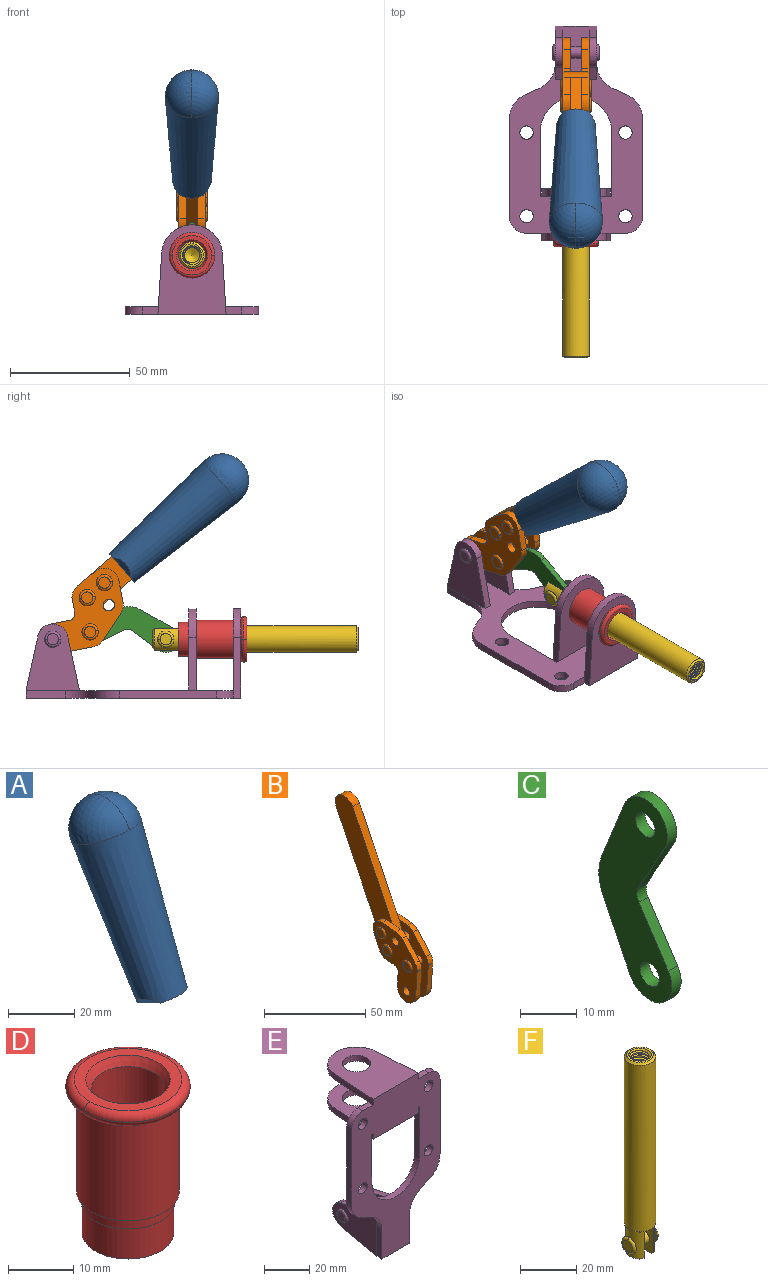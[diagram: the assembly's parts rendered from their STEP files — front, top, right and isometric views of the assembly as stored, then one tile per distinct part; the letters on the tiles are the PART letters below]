
ASSEMBLY  parts=6 mates=6
PART A: 11 faces, bbox 22.3x42.6x64.5 mm
  f0: sphere r=11.13mm, area 411.4mm2, adj f1,f8
  f1: cone r=11.11mm half-angle=3.3deg, axis (0,0.44,0.9), area 3251.8mm2, adj f0,f7,f8,f9,f10
  f2: cylinder r=6.16mm len=11.7mm, axis (1,0,0), area 89.5mm2, adj f3,f4,f5,f6
  f3: plane 60.23x36.75mm, normal (-1,0,0), area 763.6mm2, adj f2,f4,f6,f10
  f4: plane 51.37x25.05mm, normal (0,0.9,-0.44), area 264.2mm2, adj f2,f3,f5,f10
  f5: plane 60.23x36.75mm, normal (1,0,0), area 763.6mm2, adj f2,f4,f6,f10
  f6: plane 51.37x25.05mm, normal (0,-0.9,0.44), area 264.2mm2, adj f2,f3,f5,f10
  f7: plane 9.95x5.95mm, normal (0.71,-0.31,-0.64), area 25.8mm2, adj f1,f10
  f8: sphere r=11.13mm, area 411.4mm2, adj f0,f1
  f9: plane 9.95x5.95mm, normal (-0.71,-0.31,-0.64), area 25.8mm2, adj f1,f10
  f10: plane 14.27x11.38mm, normal (0,-0.44,-0.9), area 106.7mm2, adj f1,f3,f4,f5,f6,f7,f9
PART B: 59 faces, bbox 12.9x60.2x99.6 mm
  f0: torus R=2.39mm, axis (-1,0,0), area 14.9mm2, adj f20,f43,f51
  f1: torus R=2.39mm, axis (-1,0,0), area 14.9mm2, adj f19,f42,f51
  f2: torus R=2.39mm, axis (-1,0,0), area 14.9mm2, adj f18,f35,f51
  f3: torus R=2.39mm, axis (-1,0,0), area 14.9mm2, adj f14,f17,f23
  f4: torus R=2.39mm, axis (-1,0,0), area 14.9mm2, adj f13,f16,f23
  f5: torus R=2.39mm, axis (-1,0,0), area 14.9mm2, adj f12,f15,f23
  f6: cylinder r=2.39mm len=4.78mm, axis (1,0,0), area 46.5mm2, adj f48,f50,f51
  f7: cylinder r=2.39mm len=4.78mm, axis (1,0,0), area 46.5mm2, adj f50,f51
  f8: cylinder r=6.35mm len=12.68mm, axis (1,0,0), area 61.8mm2, adj f38,f39,f50,f51
  f9: cylinder r=2.39mm len=4.78mm, axis (-1,0,0), area 70.5mm2, adj f46,f50
  f10: cylinder r=2.39mm len=4.78mm, axis (-1,0,0), area 46.5mm2, adj f23,f45,f46
  f11: cylinder r=2.39mm len=4.78mm, axis (-1,0,0), area 46.5mm2, adj f23,f46
  f12: plane 4.78x4.78mm, normal (1,0,0), area 17.9mm2, adj f5,f15
  f13: plane 4.78x4.78mm, normal (1,0,0), area 17.9mm2, adj f4,f16
  f14: plane 4.78x4.78mm, normal (1,0,0), area 17.9mm2, adj f3,f17
  f15: torus R=2.39mm, axis (-1,0,0), area 14.9mm2, adj f5,f12,f23
  f16: torus R=2.39mm, axis (-1,0,0), area 14.9mm2, adj f4,f13,f23
  f17: torus R=2.39mm, axis (-1,0,0), area 14.9mm2, adj f3,f14,f23
  f18: plane 4.78x4.78mm, normal (-1,0,0), area 17.9mm2, adj f2,f35
  f19: plane 4.78x4.78mm, normal (-1,0,0), area 17.9mm2, adj f1,f42
  f20: plane 4.78x4.78mm, normal (-1,0,0), area 17.9mm2, adj f0,f43
  f21: plane 2.26x0.2mm, normal (1,0,0), area 0.2mm2, adj f31,f44
  f22: plane 2.26x0.2mm, normal (-1,0,0), area 0.2mm2, adj f41,f44
  f23: plane 39.37x30.77mm, normal (1,0,0), area 565.5mm2, adj f3,f4,f5,f10,f11,f15,f16,f17
  f24: cylinder r=6.1mm len=4.15mm, axis (-1,0,0), area 14.7mm2, adj f23,f25,f32,f46
  f25: plane 10.25x9.01mm, normal (0,-0.75,0.66), area 42.3mm2, adj f23,f24,f26,f46
  f26: cylinder r=6.35mm len=4.64mm, axis (-1,0,0), area 15.6mm2, adj f23,f25,f27,f46
  f27: plane 15.84x3.1mm, normal (0,-1,-0.07), area 49.2mm2, adj f23,f26,f28,f46
  f28: cylinder r=6.35mm len=12.68mm, axis (-1,0,0), area 61.8mm2, adj f23,f27,f29,f46
  f29: plane 8.11x3.1mm, normal (0,1,0.07), area 25.2mm2, adj f23,f28,f30,f46
  f30: cylinder r=3.05mm len=3.25mm, axis (-1,0,0), area 14.8mm2, adj f23,f29,f31,f46
  f31: plane 5.99x3.1mm, normal (0,0.07,-1), area 18.6mm2, adj f21,f23,f30,f44,f46
  f32: plane 9.5x3.1mm, normal (0,-0.07,1), area 29.5mm2, adj f23,f24,f33,f46,f47
  f33: cylinder r=6.1mm len=8.63mm, axis (-1,0,0), area 39.1mm2, adj f23,f32,f34,f47
  f34: plane 8.65x3.96mm, normal (0,0.91,-0.42), area 29.5mm2, adj f23,f33,f44,f47
  f35: torus R=2.39mm, axis (-1,0,0), area 14.9mm2, adj f2,f18,f51
  f36: plane 10.25x9.01mm, normal (0,-0.75,0.66), area 42.3mm2, adj f37,f49,f50,f51
  f37: cylinder r=6.35mm len=4.64mm, axis (1,0,0), area 15.6mm2, adj f36,f38,f50,f51
  f38: plane 15.84x3.1mm, normal (0,-1,-0.07), area 49.2mm2, adj f8,f37,f50,f51
  f39: plane 8.11x3.1mm, normal (0,1,0.07), area 25.2mm2, adj f8,f40,f50,f51
  f40: cylinder r=3.05mm len=3.25mm, axis (1,0,0), area 14.8mm2, adj f39,f41,f50,f51
  f41: plane 5.99x3.1mm, normal (0,0.07,-1), area 18.6mm2, adj f22,f40,f44,f50,f51
  f42: torus R=2.39mm, axis (-1,0,0), area 14.9mm2, adj f1,f19,f51
  f43: torus R=2.39mm, axis (-1,0,0), area 14.9mm2, adj f0,f20,f51
  f44: cylinder r=6.35mm len=12.12mm, axis (-1,0,0), area 128.9mm2, adj f21,f22,f23,f31,f34,f41,f46,f47
  f45: plane 2.65x1.35mm, normal (1,0,0), area 1mm2, adj f10,f55
  f46: plane 39.08x20.42mm, normal (-1,0,0), area 412.5mm2, adj f9,f10,f11,f24,f25,f26,f27,f28
  f47: plane 77.62x39.82mm, normal (1,0,0), area 850mm2, adj f32,f33,f34,f44,f53,f54,f55
  f48: plane 2.65x1.35mm, normal (-1,0,0), area 1mm2, adj f6,f55
  f49: cylinder r=6.1mm len=4.15mm, axis (1,0,0), area 14.7mm2, adj f36,f50,f51,f56
  f50: plane 39.08x20.42mm, normal (1,0,0), area 412.5mm2, adj f6,f7,f8,f9,f36,f37,f38,f39
  f51: plane 39.37x30.77mm, normal (-1,0,0), area 565.5mm2, adj f0,f1,f2,f6,f7,f8,f35,f36
  f52: plane 8.65x3.96mm, normal (0,0.91,-0.42), area 29.5mm2, adj f44,f51,f57,f58
  f53: plane 68.49x33.4mm, normal (0,0.9,-0.44), area 358.1mm2, adj f44,f47,f54,f58
  f54: cylinder r=6.35mm len=12.06mm, axis (1,0,0), area 93.7mm2, adj f47,f53,f55,f58
  f55: plane 68.49x33.4mm, normal (0,-0.9,0.44), area 358.1mm2, adj f44,f45,f46,f47,f48,f50,f54,f58
  f56: plane 9.5x3.1mm, normal (0,-0.07,1), area 29.5mm2, adj f49,f50,f51,f57,f58
  f57: cylinder r=6.1mm len=8.63mm, axis (1,0,0), area 39.1mm2, adj f51,f52,f56,f58
  f58: plane 77.62x39.82mm, normal (-1,0,0), area 850mm2, adj f44,f52,f53,f54,f55,f56,f57
PART C: 12 faces, bbox 2.3x18.2x42.8 mm
  f0: cylinder r=2.4mm len=4.8mm, axis (1,0,0), area 34.9mm2, adj f4,f11
  f1: cylinder r=10.41mm len=8.47mm, axis (1,0,0), area 20.2mm2, adj f4,f9,f10,f11
  f2: cylinder r=3.05mm len=3.16mm, axis (1,0,0), area 7.7mm2, adj f4,f6,f7,f11
  f3: cylinder r=2.4mm len=4.8mm, axis (1,0,0), area 34.9mm2, adj f4,f11
  f4: plane 42.81x18.23mm, normal (-1,0,0), area 414.1mm2, adj f0,f1,f2,f3,f5,f6,f7,f8
  f5: cylinder r=5.54mm len=10.67mm, axis (1,0,0), area 41.8mm2, adj f4,f6,f10,f11
  f6: plane 11.66x6.53mm, normal (0,-0.87,-0.49), area 30.9mm2, adj f2,f4,f5,f11
  f7: plane 11.17x7.33mm, normal (0,-0.84,0.55), area 30.9mm2, adj f2,f4,f8,f11
  f8: cylinder r=5.54mm len=10.51mm, axis (1,0,0), area 41.8mm2, adj f4,f7,f9,f11
  f9: plane 13.67x6.67mm, normal (0,0.9,-0.44), area 35.1mm2, adj f1,f4,f8,f11
  f10: plane 14.1x5.7mm, normal (0,0.93,0.37), area 35.1mm2, adj f1,f4,f5,f11
  f11: plane 42.81x18.23mm, normal (1,0,0), area 414.1mm2, adj f0,f1,f2,f3,f5,f6,f7,f8
PART D: 15 faces, bbox 20.6x20.6x28.7 mm
  f0: torus R=8.26mm, axis (0,0,1), area 56.8mm2, adj f1,f10,f12
  f1: torus R=8.26mm, axis (0,0,1), area 56.8mm2, adj f0,f6,f13
  f2: cylinder r=5.59mm len=25.91mm, axis (0,0,1), area 909.6mm2, adj f3,f4
  f3: cone r=6.86mm half-angle=45deg, axis (0,0,-1), area 70.2mm2, adj f2,f14
  f4: cone r=6.47mm half-angle=30deg, axis (0,0,1), area 66.7mm2, adj f2,f13
  f5: cylinder r=7.04mm len=14.07mm, axis (0,0,1), area 252.6mm2, adj f11,f14
  f6: torus R=8.26mm, axis (0,0,1), area 56.8mm2, adj f1,f12,f13
  f7: cylinder r=7.16mm len=14.33mm, axis (0,0,1), area 91.5mm2, adj f9,f11
  f8: cylinder r=7.86mm len=18.42mm, axis (0,0,1), area 909.6mm2, adj f9,f10
  f9: plane 15.72x15.72mm, normal (0,0,-1), area 33mm2, adj f7,f8
  f10: plane 16.51x16.51mm, normal (0,0,-1), area 19.9mm2, adj f0,f8,f12
  f11: plane 14.33x14.33mm, normal (0,0,-1), area 5.7mm2, adj f5,f7
  f12: torus R=8.26mm, axis (0,0,1), area 56.8mm2, adj f0,f6,f10
  f13: plane 16.51x16.51mm, normal (0,0,1), area 82.7mm2, adj f1,f4,f6
  f14: plane 14.07x14.07mm, normal (0,0,-1), area 7.8mm2, adj f3,f5
PART E: 55 faces, bbox 55.7x37.4x89.8 mm
  f0: torus R=2.41mm, axis (-1,0,0), area 15mm2, adj f11,f15,f25
  f1: torus R=2.41mm, axis (-1,0,0), area 15mm2, adj f10,f12,f22
  f2: cylinder r=2.78mm len=5.56mm, axis (0,-1,0), area 54.2mm2, adj f30,f54
  f3: cylinder r=14.99mm len=29.97mm, axis (0,-1,0), area 145.9mm2, adj f30,f49,f53,f54
  f4: cylinder r=2.78mm len=5.56mm, axis (0,-1,0), area 54.2mm2, adj f30,f54
  f5: cylinder r=2.78mm len=5.56mm, axis (0,-1,0), area 54.2mm2, adj f30,f54
  f6: cylinder r=2.78mm len=5.56mm, axis (0,-1,0), area 54.2mm2, adj f30,f54
  f7: cylinder r=6.35mm len=12.7mm, axis (0,0,1), area 123.6mm2, adj f27,f51
  f8: cylinder r=6.35mm len=12.7mm, axis (0,0,-1), area 124.7mm2, adj f21,f35
  f9: cylinder r=2.41mm len=11.18mm, axis (-1,0,0), area 169.4mm2, adj f16,f19
  f10: plane 4.83x4.83mm, normal (1,0,0), area 18.3mm2, adj f1,f12
  f11: plane 4.83x4.83mm, normal (-1,0,0), area 18.3mm2, adj f0,f15
  f12: torus R=2.41mm, axis (-1,0,0), area 15mm2, adj f1,f10,f22
  f13: cylinder r=6.35mm len=12.41mm, axis (1,0,0), area 53.4mm2, adj f18,f19,f22,f23
  f14: cylinder r=6.35mm len=12.41mm, axis (-1,0,0), area 53.4mm2, adj f16,f17,f24,f25
  f15: torus R=2.41mm, axis (-1,0,0), area 15mm2, adj f0,f11,f25
  f16: plane 27.86x22.35mm, normal (1,0,0), area 425.4mm2, adj f9,f14,f17,f24,f30
  f17: plane 22.86x4.97mm, normal (0,0.21,0.98), area 72.5mm2, adj f14,f16,f25,f30
  f18: plane 22.86x4.97mm, normal (0,0.21,0.98), area 72.5mm2, adj f13,f19,f22,f30
  f19: plane 27.86x22.35mm, normal (-1,0,0), area 425.4mm2, adj f9,f13,f18,f23,f30
  f20: cylinder r=12.7mm len=25.35mm, axis (0,0,-1), area 119.8mm2, adj f21,f34,f35,f36
  f21: plane 34.21x28.07mm, normal (0,0,-1), area 702.4mm2, adj f8,f20,f30,f34,f36
  f22: plane 27.96x22.45mm, normal (1,0,0), area 407.2mm2, adj f1,f12,f13,f18,f23,f30,f42,f43
  f23: plane 22.86x4.97mm, normal (0,0.21,-0.98), area 72.5mm2, adj f13,f19,f22,f44
  f24: plane 22.86x4.97mm, normal (0,0.21,-0.98), area 72.5mm2, adj f14,f16,f25,f44
  f25: plane 27.86x22.35mm, normal (-1,0,0), area 407.1mm2, adj f0,f14,f15,f17,f24,f30,f45,f46
  f26: plane 3.1x0.95mm, normal (0,0,-1), area 2.7mm2, adj f30,f49,f50,f54
  f27: plane 34.21x28.07mm, normal (0,0,1), area 702.4mm2, adj f7,f28,f30,f50,f52
  f28: cylinder r=12.7mm len=25.35mm, axis (0,0,1), area 118.8mm2, adj f27,f50,f51,f52
  f29: plane 3.1x0.95mm, normal (0,0,-1), area 2.7mm2, adj f30,f52,f53,f54
  f30: plane 86.54x55.63mm, normal (0,1,0), area 2362.9mm2, adj f2,f3,f4,f5,f6,f16,f17,f18
  f31: plane 40.56x3.1mm, normal (-1,0,0), area 125.7mm2, adj f30,f32,f48,f54
  f32: cylinder r=7.11mm len=7.11mm, axis (0,-1,0), area 34.6mm2, adj f30,f31,f33,f54
  f33: plane 6.67x3.1mm, normal (0,0,1), area 20.4mm2, adj f30,f32,f34,f54
  f34: plane 25.39x3.13mm, normal (-1,0.06,0), area 79.5mm2, adj f20,f21,f33,f35,f54
  f35: plane 37.31x28.45mm, normal (0,0,1), area 789.9mm2, adj f8,f20,f34,f36,f54
  f36: plane 25.39x3.13mm, normal (1,0.06,0), area 79.5mm2, adj f20,f21,f35,f37,f54
  f37: plane 6.67x3.1mm, normal (0,0,1), area 20.4mm2, adj f30,f36,f38,f54
  f38: cylinder r=7.11mm len=7.11mm, axis (0,-1,0), area 34.6mm2, adj f30,f37,f39,f54
  f39: plane 40.56x3.1mm, normal (1,0,0), area 125.7mm2, adj f30,f38,f40,f54
  f40: cylinder r=11.18mm len=10.16mm, axis (0,-1,0), area 39.5mm2, adj f30,f39,f41,f54
  f41: plane 6.09x3.1mm, normal (0.42,0,-0.91), area 20.8mm2, adj f30,f40,f42,f54
  f42: cylinder r=11.18mm len=9.41mm, axis (0,-1,0), area 37.2mm2, adj f22,f30,f41,f43,f54
  f43: plane 16.5x3.1mm, normal (1,0,0), area 51.1mm2, adj f22,f42,f44,f54
  f44: plane 17.37x3.1mm, normal (0,0,-1), area 53.8mm2, adj f23,f24,f30,f43,f45,f54
  f45: plane 16.5x3.1mm, normal (-1,0,0), area 51.1mm2, adj f25,f44,f46,f54
  f46: cylinder r=11.18mm len=9.41mm, axis (0,-1,0), area 37.2mm2, adj f25,f30,f45,f47,f54
  f47: plane 6.09x3.1mm, normal (-0.42,0,-0.91), area 20.8mm2, adj f30,f46,f48,f54
  f48: cylinder r=11.18mm len=10.16mm, axis (0,-1,0), area 39.5mm2, adj f30,f31,f47,f54
  f49: plane 26.54x3.1mm, normal (-1,0,0), area 82.3mm2, adj f3,f26,f30,f54
  f50: plane 25.39x3.1mm, normal (1,0.06,0), area 78.8mm2, adj f26,f27,f28,f51,f54
  f51: plane 37.31x28.45mm, normal (0,0,-1), area 789.9mm2, adj f7,f28,f50,f52,f54
  f52: plane 25.39x3.1mm, normal (-1,0.06,0), area 78.8mm2, adj f27,f28,f29,f51,f54
  f53: plane 26.54x3.1mm, normal (1,0,0), area 82.3mm2, adj f3,f29,f30,f54
  f54: plane 89.66x55.63mm, normal (0,-1,0), area 2678.5mm2, adj f2,f3,f4,f5,f6,f26,f29,f31
PART F: 48 faces, bbox 12.6x11.1x86.1 mm
  f0: torus R=2.41mm, axis (-1,0,0), area 15mm2, adj f30,f32,f34
  f1: torus R=2.41mm, axis (-1,0,0), area 15mm2, adj f29,f31,f33
  f2: cylinder r=5.54mm len=72.39mm, axis (0,0,1), area 2518.5mm2, adj f3,f4,f42,f43
  f3: cone r=5.54mm half-angle=45deg, axis (0,0,1), area 7.6mm2, adj f2,f5,f41
  f4: cone r=5.54mm half-angle=45deg, axis (0,0,-1), area 34.9mm2, adj f2,f39
  f5: cylinder r=5.08mm len=11.48mm, axis (0,0,1), area 108.3mm2, adj f3,f7,f8,f41
  f6: cylinder r=2.41mm len=4.83mm, axis (-1,0,0), area 71.2mm2, adj f40,f41
  f7: cylinder r=2.41mm len=4.83mm, axis (-1,0,0), area 7.6mm2, adj f5,f34
  f8: cone r=5.08mm half-angle=45deg, axis (0,0,1), area 10.6mm2, adj f5,f37,f41
  f9: cone r=3.98mm half-angle=45deg, axis (0,0,1), area 17.6mm2, adj f27,f39,f45,f46,f47
  f10: cylinder r=2.41mm len=4.83mm, axis (-1,0,0), area 7.6mm2, adj f33,f38
  f11: cylinder r=3.2mm len=6.4mm, axis (0,0,1), area 78.4mm2, adj f12,f28,f44,f45,f47
  f12: cylinder r=3.2mm len=6.4mm, axis (0,0,1), area 10.5mm2, adj f11,f13,f45,f47
  f13: cylinder r=3.2mm len=6.4mm, axis (0,0,1), area 10.5mm2, adj f12,f14,f45,f47
  f14: cylinder r=3.2mm len=6.4mm, axis (0,0,1), area 10.5mm2, adj f13,f15,f45,f47
  f15: cylinder r=3.2mm len=6.4mm, axis (0,0,1), area 10.5mm2, adj f14,f16,f45,f47
  f16: cylinder r=3.2mm len=6.4mm, axis (0,0,1), area 10.5mm2, adj f15,f17,f45,f47
  f17: cylinder r=3.2mm len=6.4mm, axis (0,0,1), area 10.5mm2, adj f16,f18,f45,f47
  f18: cylinder r=3.2mm len=6.4mm, axis (0,0,1), area 10.5mm2, adj f17,f19,f45,f47
  f19: cylinder r=3.2mm len=6.4mm, axis (0,0,1), area 10.5mm2, adj f18,f20,f45,f47
  f20: cylinder r=3.2mm len=6.4mm, axis (0,0,1), area 10.5mm2, adj f19,f21,f45,f47
  f21: cylinder r=3.2mm len=6.4mm, axis (0,0,1), area 10.5mm2, adj f20,f22,f45,f47
  f22: cylinder r=3.2mm len=6.4mm, axis (0,0,1), area 10.5mm2, adj f21,f23,f45,f47
  f23: cylinder r=3.2mm len=6.4mm, axis (0,0,1), area 10.5mm2, adj f22,f24,f45,f47
  f24: cylinder r=3.2mm len=6.4mm, axis (0,0,1), area 10.5mm2, adj f23,f25,f45,f47
  f25: cylinder r=3.2mm len=6.4mm, axis (0,0,1), area 10.5mm2, adj f24,f26,f45,f47
  f26: cylinder r=3.2mm len=6.4mm, axis (0,0,1), area 10.5mm2, adj f25,f27,f45,f47
  f27: cylinder r=3.2mm len=6.4mm, axis (0,0,1), area 7.4mm2, adj f9,f26,f45,f47
  f28: cone r=3.2mm half-angle=60deg, axis (0,0,1), area 37.2mm2, adj f11
  f29: plane 4.83x4.83mm, normal (-1,0,0), area 18.3mm2, adj f1,f31
  f30: plane 4.83x4.83mm, normal (1,0,0), area 18.3mm2, adj f0,f32
  f31: torus R=2.41mm, axis (-1,0,0), area 15mm2, adj f1,f29,f33
  f32: torus R=2.41mm, axis (-1,0,0), area 15mm2, adj f0,f30,f34
  f33: plane 6.83x6.83mm, normal (1,0,0), area 18.3mm2, adj f1,f10,f31
  f34: plane 6.83x6.83mm, normal (-1,0,0), area 18.3mm2, adj f0,f7,f32
  f35: cone r=5.08mm half-angle=45deg, axis (0,0,1), area 10.6mm2, adj f36,f38,f40
  f36: plane 7.25x1.97mm, normal (0,0,-1), area 10mm2, adj f35,f40
  f37: plane 7.25x1.97mm, normal (0,0,-1), area 10mm2, adj f8,f41
  f38: cylinder r=5.08mm len=11.48mm, axis (0,0,1), area 108.3mm2, adj f10,f35,f40,f42
  f39: plane 9.55x9.55mm, normal (0,0,1), area 22mm2, adj f4,f9
  f40: plane 12.76x10.09mm, normal (1,0,0), area 95.7mm2, adj f6,f35,f36,f38,f42,f43
  f41: plane 12.76x10.09mm, normal (-1,0,0), area 95.7mm2, adj f3,f5,f6,f8,f37,f43
  f42: cone r=5.54mm half-angle=45deg, axis (0,0,1), area 7.6mm2, adj f2,f38,f40
  f43: plane 11.07x4.7mm, normal (0,0,-1), area 50.4mm2, adj f2,f40,f41
  f44: plane 0.89x0.62mm, normal (-1,0,0), area 0.3mm2, adj f11,f45,f46,f47
  f45: bspline ~24.8x7.63mm, area 266.6mm2, adj f9,f11,f12,f13,f14,f15,f16,f17
  f46: bspline ~24.87x7.63mm, area 73.6mm2, adj f9,f44,f45,f47
  f47: bspline ~24.98x7.63mm, area 272.5mm2, adj f9,f11,f12,f13,f14,f15,f16,f17
PLACE A rot(axis=(1,0,0),75deg) t=(-0.04,3.86,9.14)mm
PLACE B rot(axis=(1,0,0),75deg) t=(0,3.86,9.14)mm
PLACE C rot(axis=(1,0,0),97.5deg) t=(0,12.59,2.22)mm
PLACE D rot(axis=(1,0,0),90deg) t=(0,9.14,0)mm
PLACE E rot(axis=(1,0,0),90deg) t=(0,9.14,0)mm fixed
PLACE F rot(axis=(1,0,0),90deg) t=(0,9.52,0)mm
MATE fastened D.f0 <-> E.f7  axis (0,1,0) through (0,-37.25,24.61)mm
MATE fastened A.f2 <-> B.f54  axis (1,0,0) through (-2.35,-30.66,91.94)mm
MATE slider F.f2 <-> D.f2  axis (0,-1,0) through (0,-49.26,24.61)mm
MATE revolute C.f5 <-> F.f6  axis (1,0,0) through (0,-5.96,24.61)mm
MATE revolute E.f0 <-> B.f7  axis (-1,0,0) through (0,41.23,24.61)mm
MATE revolute C.f3 <-> B.f4  axis (1,0,0) through (0,25.65,27.64)mm
